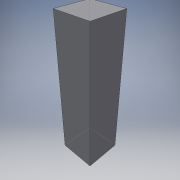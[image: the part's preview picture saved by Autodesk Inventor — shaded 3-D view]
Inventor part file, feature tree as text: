
AUTODESK INVENTOR PART (.ipt)
format: ipt  version: 2016 (Build 200138000, 138)  size: 87,040 bytes
history: native  units: in
note: dims shown in document units (in); Inventor stores cm internally (conversion verified against a paired STEP export)
features: extrude x1, sketch x1
ambient origin geometry x8: Origin, YZ Plane, XZ Plane, XY Plane, X Axis, Y Axis, Z Axis, Center Point
bodies: Solid1 (feature_tree)
feature tree (2):
  extrude  "Extrusion1"  Depth=1.5in
  sketch  "Sketch1"  dims[d0=1.5in d1=1.5in d2=5.75in d3=0.0in]
